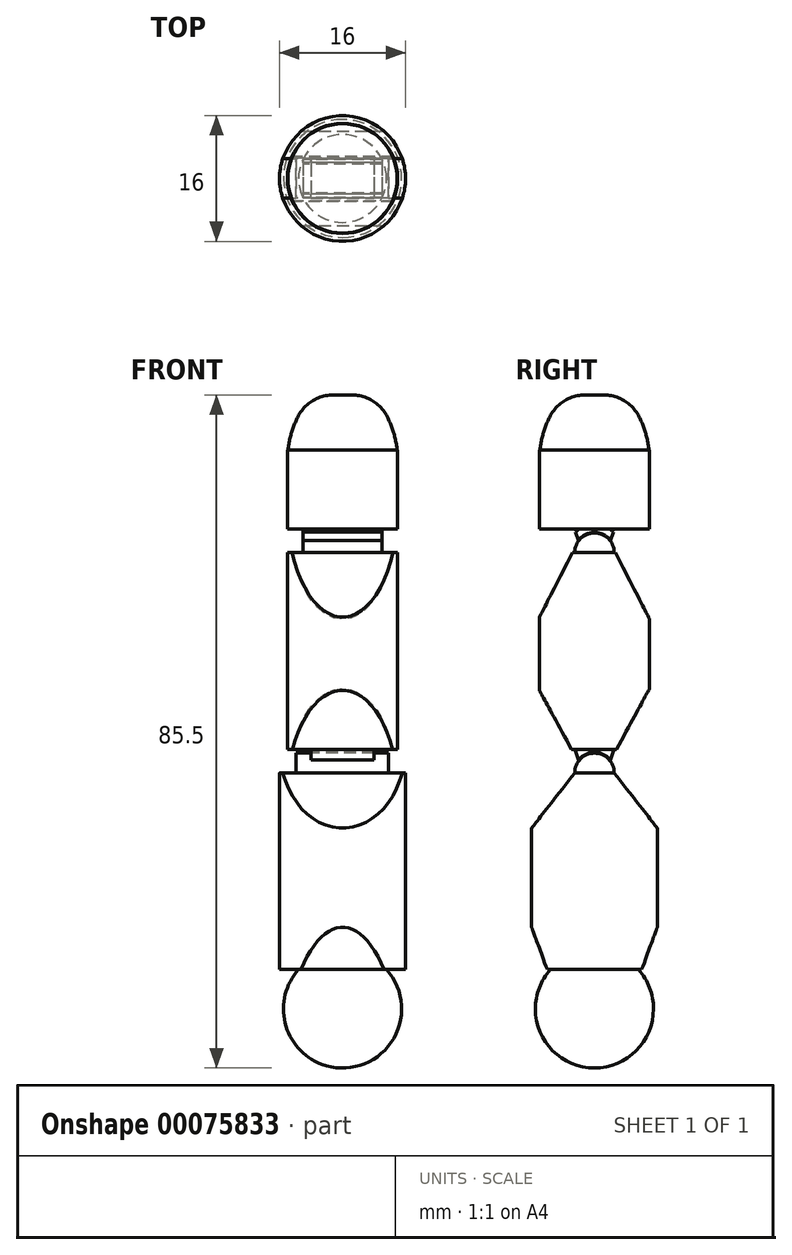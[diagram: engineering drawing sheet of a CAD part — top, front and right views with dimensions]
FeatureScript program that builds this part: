
annotation { "Feature Type Name" : "Feature", "Feature Type Description" : "" }
export const myFeature = defineFeature(function(context is Context, id is Id, definition is map)
    precondition{}
    {
        {
            var Q0;
            Q0=qCreatedBy(makeId("Top.planeOp"),FACE);
            var sketch = newSketch(context, id + "F0", { "sketchPlane" : qUnion([Q0])});
            skArc(sketch, "E0", {"start": v(0, 7.5) * mm, "mid": v(-7.5, 0) * mm, "end": v(0, -7.5) * mm});
            skLineSegment(sketch, "E1", {"start": v(0, 7.5) * mm, "end": v(0, -7.5) * mm});
            skSolve(sketch);
        }
        {
            var Q0;
            Q0=qSketchRegion(id+"F0",true);
            var Q1;
            Q1=sQuery(id+"F0.wireOp",EDGE,"E1");
            revolve(context, id + "F1", {"entities" : qUnion([Q0]), "axis" : qUnion([Q1]), "revolveType" : RevolveType.FULL});
        }
        {
            var Q0;
            Q0=qCreatedBy(makeId("Top.planeOp"),FACE);
            cPlane(context, id + "F2", {"entities" : qUnion([Q0]), "cplaneType" : CPlaneType.OFFSET, "offset" : 5 * mm, "width" : 150 * mm, "height" : 150 * mm});
        }
        {
            var Q0;
            Q0=qCreatedBy(id+"F2.planeOp",FACE);
            var sketch = newSketch(context, id + "F3", { "sketchPlane" : qUnion([Q0])});
            skCircle(sketch, "E2", {"center": v(0, 0) * mm, "radius": 8 * mm});
            skSolve(sketch);
        }
        {
            var Q0;
            Q0=qSketchRegion(id+"F3",true);
            extrude(context, id + "F4", {"entities" : qUnion([Q0]), "operationType" : NewBodyOperationType.ADD, "depth" : 25 * mm});
        }
        {
            var Q0;
            Q0=qCreatedBy(makeId("Right.planeOp"),FACE);
            var sketch = newSketch(context, id + "F5", { "sketchPlane" : qUnion([Q0])});
            skCircle(sketch, "E3", {"center": v(0, 30) * mm, "radius": 2.5 * mm});
            skSolve(sketch);
        }
        {
            var Q0;
            Q0=makeQuery(id+"F5.imprint","IMPRINT",FACE,{"disambiguationData":[TD([[makeQuery(id+"F5.imprint","IMPRINT",EDGE,{"derivedFrom":sQuery(id+"F5.wireOp",EDGE,"E3")}),1.0]])]});
            var Q1;
            Q1=sQuery(id+"F5.wireOp",EDGE,"E3");
            extrude(context, id + "F6", {"entities" : qUnion([Q0]), "operationType" : NewBodyOperationType.ADD, "surfaceEntities" : qUnion([Q1]), "depth" : 5.85 * mm, "hasSecondDirection" : true, "secondDirectionOppositeDirection" : true, "secondDirectionDepth" : 5.9 * mm});
        }
        {
            var Q0;
            Q0=qCreatedBy(makeId("Right.planeOp"),FACE);
            var sketch = newSketch(context, id + "F7", { "sketchPlane" : qUnion([Q0])});
            skLineSegment(sketch, "E4", {"start": v(2.5, 30) * mm, "end": v(10.5, 19.75) * mm});
            skLineSegment(sketch, "E5", {"start": v(10.5, 19.75) * mm, "end": v(10.5, 30) * mm});
            skLineSegment(sketch, "E6", {"start": v(10.5, 30) * mm, "end": v(2.5, 30) * mm});
            skLineSegment(sketch, "E7", {"start": v(-2.5, 30) * mm, "end": v(-10.5, 30) * mm});
            skLineSegment(sketch, "E8", {"start": v(-10.5, 30) * mm, "end": v(-10.5, 19.75) * mm});
            skLineSegment(sketch, "E9", {"start": v(-10.5, 19.75) * mm, "end": v(-2.5, 30) * mm});
            skLineSegment(sketch, "E10", {"start": v(-10.5, 5) * mm, "end": v(-6, 5) * mm});
            skLineSegment(sketch, "E11", {"start": v(-6, 5) * mm, "end": v(-10.5, 17.2) * mm});
            skLineSegment(sketch, "E12", {"start": v(-10.5, 17.2) * mm, "end": v(-10.5, 5) * mm});
            skLineSegment(sketch, "E13", {"start": v(6, 5) * mm, "end": v(10.5, 5) * mm});
            skLineSegment(sketch, "E14", {"start": v(10.5, 5) * mm, "end": v(10.5, 17.2) * mm});
            skLineSegment(sketch, "E15", {"start": v(10.5, 17.2) * mm, "end": v(6, 5) * mm});
            skSolve(sketch);
        }
        {
            var Q0;
            Q0=qSketchRegion(id+"F7",true);
            extrude(context, id + "F8", {"entities" : qUnion([Q0]), "operationType" : NewBodyOperationType.REMOVE, "oppositeDirection" : true, "depth" : 25 * mm, "hasSecondDirection" : true, "secondDirectionOppositeDirection" : false, "secondDirectionDepth" : 25 * mm});
        }
        {
            var Q0;
            Q0=qCreatedBy(makeId("Right.planeOp"),FACE);
            var sketch = newSketch(context, id + "F9", { "sketchPlane" : qUnion([Q0])});
            skArc(sketch, "E16", {"start": v(2.6, 30) * mm, "mid": v(0, 32.6) * mm, "end": v(-2.6, 30) * mm});
            skLineSegment(sketch, "E17", {"start": v(-2.6, 30) * mm, "end": v(-4, 30) * mm});
            skLineSegment(sketch, "E18", {"start": v(2.6, 30) * mm, "end": v(4, 30) * mm});
            skArc(sketch, "E19", {"start": v(4, 30) * mm, "mid": v(0, 34) * mm, "end": v(-4, 30) * mm});
            skLineSegment(sketch, "E20", {"start": v(0, 32.6) * mm, "end": v(0, 34) * mm, "construction": true});
            skSolve(sketch);
        }
        {
            var Q0;
            Q0=qSketchRegion(id+"F9",true);
            extrude(context, id + "F10", {"entities" : qUnion([Q0]), "depth" : 4 * mm, "hasSecondDirection" : true, "secondDirectionOppositeDirection" : true, "secondDirectionDepth" : 4 * mm});
        }
        {
            var Q0;
            Q0=qCreatedBy(makeId("Right.planeOp"),FACE);
            var sketch = newSketch(context, id + "F11", { "sketchPlane" : qUnion([Q0])});
            skLineSegment(sketch, "E21", {"start": v(0, 33) * mm, "end": v(0, 57.97) * mm});
            skLineSegment(sketch, "E22", {"start": v(0, 57.97) * mm, "end": v(-7, 57.97) * mm});
            skLineSegment(sketch, "E23", {"start": v(-7, 57.97) * mm, "end": v(-7, 32.97) * mm});
            skLineSegment(sketch, "E24", {"start": v(-7, 32.97) * mm, "end": v(0, 33) * mm});
            skSolve(sketch);
        }
        {
            var Q0;
            Q0=makeQuery(id+"F11.imprint","IMPRINT",FACE,{"disambiguationData":[TD([[makeQuery(id+"F11.imprint","IMPRINT",EDGE,{"derivedFrom":sQuery(id+"F11.wireOp",EDGE,"E21")}),1.0]])]});
            var Q1;
            Q1=sQuery(id+"F11.wireOp",EDGE,"E21");
            revolve(context, id + "F12", {"operationType" : NewBodyOperationType.ADD, "entities" : qUnion([Q0]), "axis" : qUnion([Q1]), "revolveType" : RevolveType.FULL});
        }
        {
            var Q0;
            Q0=makeQuery(id+"F10.opExtrude","SWEPT_EDGE",EDGE,{"disambiguationData":[OSD([sQuery(id+"F9.wireOp",EDGE,"E17"),sQuery(id+"F9.wireOp",EDGE,"E19")])]});
            var Q1;
            Q1=makeQuery(id+"F10.opExtrude","SWEPT_EDGE",EDGE,{"disambiguationData":[OSD([sQuery(id+"F9.wireOp",EDGE,"E18"),sQuery(id+"F9.wireOp",EDGE,"E19")])]});
            chamfer(context, id + "F13", {"entities" : qUnion([Q0, Q1]), "width" : 1.75 * mm, "tangentPropagation" : true});
        }
        {
            var Q0;
            Q0=qCreatedBy(makeId("Right.planeOp"),FACE);
            var sketch = newSketch(context, id + "F14", { "sketchPlane" : qUnion([Q0])});
            skArc(sketch, "E25", {"start": v(2.5, 57.97) * mm, "mid": v(0, 60.47) * mm, "end": v(-2.5, 57.97) * mm});
            skLineSegment(sketch, "E26", {"start": v(2.5, 57.97) * mm, "end": v(-2.5, 57.97) * mm});
            skPoint(sketch, "E27", {"position": v(2.5, 57.97) * mm});
            skSolve(sketch);
        }
        {
            var Q0;
            Q0=qSketchRegion(id+"F14",true);
            extrude(context, id + "F15", {"entities" : qUnion([Q0]), "operationType" : NewBodyOperationType.ADD, "depth" : 5 * mm, "hasSecondDirection" : true, "secondDirectionOppositeDirection" : true, "secondDirectionDepth" : 5 * mm});
        }
        {
            var Q0;
            Q0=qCreatedBy(makeId("Right.planeOp"),FACE);
            var sketch = newSketch(context, id + "F16", { "sketchPlane" : qUnion([Q0])});
            skLineSegment(sketch, "E28", {"start": v(-2.9, 32.97) * mm, "end": v(-7.19, 40.83) * mm});
            skLineSegment(sketch, "E29", {"start": v(-7.19, 40.83) * mm, "end": v(-7.19, 32.97) * mm});
            skLineSegment(sketch, "E30", {"start": v(-7.19, 32.97) * mm, "end": v(-2.9, 32.97) * mm});
            skLineSegment(sketch, "E31", {"start": v(2.79, 32.97) * mm, "end": v(7.07, 40.83) * mm});
            skLineSegment(sketch, "E32", {"start": v(7.07, 40.83) * mm, "end": v(7.07, 32.97) * mm});
            skLineSegment(sketch, "E33", {"start": v(7.07, 32.97) * mm, "end": v(2.79, 32.97) * mm});
            skLineSegment(sketch, "E34", {"start": v(-2.78, 57.97) * mm, "end": v(-7.19, 57.97) * mm});
            skLineSegment(sketch, "E35", {"start": v(-7.19, 57.97) * mm, "end": v(-7.19, 49.39) * mm});
            skLineSegment(sketch, "E36", {"start": v(-7.19, 49.39) * mm, "end": v(-2.78, 57.97) * mm});
            skLineSegment(sketch, "E37", {"start": v(2.66, 57.97) * mm, "end": v(7.07, 57.97) * mm});
            skLineSegment(sketch, "E38", {"start": v(7.07, 57.97) * mm, "end": v(7.07, 49.39) * mm});
            skLineSegment(sketch, "E39", {"start": v(7.07, 49.39) * mm, "end": v(2.66, 57.97) * mm});
            skSolve(sketch);
        }
        {
            var Q0;
            Q0=qSketchRegion(id+"F16",true);
            extrude(context, id + "F17", {"entities" : qUnion([Q0]), "operationType" : NewBodyOperationType.REMOVE, "oppositeDirection" : true, "depth" : 25 * mm, "hasSecondDirection" : true, "secondDirectionOppositeDirection" : false, "secondDirectionDepth" : 25 * mm});
        }
        {
            var Q0;
            Q0=qCreatedBy(makeId("Right.planeOp"),FACE);
            var sketch = newSketch(context, id + "F18", { "sketchPlane" : qUnion([Q0])});
            skArc(sketch, "E40", {"start": v(2.55, 57.97) * mm, "mid": v(0, 60.52) * mm, "end": v(-2.55, 57.97) * mm});
            skPoint(sketch, "E41", {"position": v(-2.55, 57.97) * mm});
            skLineSegment(sketch, "E42", {"start": v(-2.55, 57.97) * mm, "end": v(-3.55, 57.97) * mm});
            skLineSegment(sketch, "E43", {"start": v(2.55, 57.97) * mm, "end": v(3.55, 57.97) * mm});
            skLineSegment(sketch, "E44", {"start": v(0, 60.52) * mm, "end": v(0, 61.52) * mm, "construction": true});
            skPoint(sketch, "E44.endSnap0", {"position": v(0, 60.52) * mm});
            skArc(sketch, "E45", {"start": v(3.55, 57.97) * mm, "mid": v(0, 61.52) * mm, "end": v(-3.55, 57.97) * mm});
            skSolve(sketch);
        }
        {
            var Q0;
            Q0=qSketchRegion(id+"F18",true);
            extrude(context, id + "F19", {"entities" : qUnion([Q0]), "depth" : 5 * mm, "hasSecondDirection" : true, "secondDirectionOppositeDirection" : true, "secondDirectionDepth" : 5 * mm});
        }
        {
            var Q0;
            Q0=qCreatedBy(makeId("Right.planeOp"),FACE);
            var sketch = newSketch(context, id + "F20", { "sketchPlane" : qUnion([Q0])});
            skLineSegment(sketch, "E46", {"start": v(0, 61) * mm, "end": v(0, 71) * mm});
            skLineSegment(sketch, "E47", {"start": v(0, 71) * mm, "end": v(-7, 71) * mm});
            skLineSegment(sketch, "E48", {"start": v(-7, 71) * mm, "end": v(-7, 61) * mm});
            skLineSegment(sketch, "E49", {"start": v(-7, 61) * mm, "end": v(0, 61) * mm});
            skSolve(sketch);
        }
        {
            var Q0;
            Q0=makeQuery(id+"F20.imprint","IMPRINT",FACE,{"disambiguationData":[TD([[makeQuery(id+"F20.imprint","IMPRINT",EDGE,{"derivedFrom":sQuery(id+"F20.wireOp",EDGE,"E46")}),1.0]])]});
            var Q1;
            Q1=sQuery(id+"F20.wireOp",EDGE,"E46");
            revolve(context, id + "F21", {"operationType" : NewBodyOperationType.ADD, "entities" : qUnion([Q0]), "axis" : qUnion([Q1]), "revolveType" : RevolveType.FULL});
        }
        {
            var Q0;
            Q0=qCreatedBy(makeId("Right.planeOp"),FACE);
            var sketch = newSketch(context, id + "F22", { "sketchPlane" : qUnion([Q0])});
            skLineSegment(sketch, "E50", {"start": v(0, 71) * mm, "end": v(0, 81) * mm});
            skArc(sketch, "E51", {"start": v(0, 81) * mm, "mid": v(-4.71, 76.86) * mm, "end": v(-6.94, 71) * mm});
            skLineSegment(sketch, "E52", {"start": v(0, 71) * mm, "end": v(-6.94, 71) * mm});
            skSolve(sketch);
        }
        {
            var Q0;
            Q0=makeQuery(id+"F22.imprint","IMPRINT",FACE,{"disambiguationData":[TD([[makeQuery(id+"F22.imprint","IMPRINT",EDGE,{"derivedFrom":sQuery(id+"F22.wireOp",EDGE,"E50")}),1.0]])]});
            var Q1;
            Q1=sQuery(id+"F22.wireOp",EDGE,"E50");
            revolve(context, id + "F23", {"operationType" : NewBodyOperationType.ADD, "entities" : qUnion([Q0]), "axis" : qUnion([Q1]), "revolveType" : RevolveType.FULL});
        }
        {
            var Q0;
            Q0=qCreatedBy(makeId("Right.planeOp"),FACE);
            var sketch = newSketch(context, id + "F24", { "sketchPlane" : qUnion([Q0])});
            skLineSegment(sketch, "E53.bottom", {"start": v(-5, 81) * mm, "end": v(5, 81) * mm});
            skLineSegment(sketch, "E53.top", {"start": v(-5, 78) * mm, "end": v(5, 78) * mm});
            skLineSegment(sketch, "E53.left", {"start": v(-5, 81) * mm, "end": v(-5, 78) * mm});
            skLineSegment(sketch, "E53.right", {"start": v(5, 81) * mm, "end": v(5, 78) * mm});
            skPoint(sketch, "E54", {"position": v(0, 81) * mm});
            skSolve(sketch);
        }
        {
            var Q0;
            Q0=qSketchRegion(id+"F24",true);
            extrude(context, id + "F25", {"entities" : qUnion([Q0]), "operationType" : NewBodyOperationType.REMOVE, "oppositeDirection" : true, "depth" : 25 * mm, "hasSecondDirection" : true, "secondDirectionOppositeDirection" : false, "secondDirectionDepth" : 25 * mm});
        }
        {
            var Q0;
            Q0=makeQuery(id+"F25.boolean.opBoolean","INTERSECT",EDGE,{"derivedFrom":[makeQuery(id+"F23.opRevolve","SWEPT_FACE",FACE,{"disambiguationData":[OSD([sQuery(id+"F22.wireOp",EDGE,"E51")])]}),makeQuery(id+"F25.opExtrude","SWEPT_FACE",FACE,{"disambiguationData":[OSD([sQuery(id+"F24.wireOp",EDGE,"E53.top")])]})]});
            fillet(context, id + "F26", {"entities" : qUnion([Q0]), "radius" : 5 * mm, "tangentPropagation" : true, "allowEdgeOverflow" : false});
        }
        {
            var Q0;
            Q0=makeQuery(id+"F19.opExtrude","SWEPT_EDGE",EDGE,{"disambiguationData":[OSD([sQuery(id+"F18.wireOp",EDGE,"E42"),sQuery(id+"F18.wireOp",EDGE,"E45")])]});
            var Q1;
            Q1=makeQuery(id+"F19.opExtrude","SWEPT_EDGE",EDGE,{"disambiguationData":[OSD([sQuery(id+"F18.wireOp",EDGE,"E43"),sQuery(id+"F18.wireOp",EDGE,"E45")])]});
            chamfer(context, id + "F27", {"entities" : qUnion([Q0, Q1]), "width" : 1.5 * mm, "tangentPropagation" : true});
        }
    });
